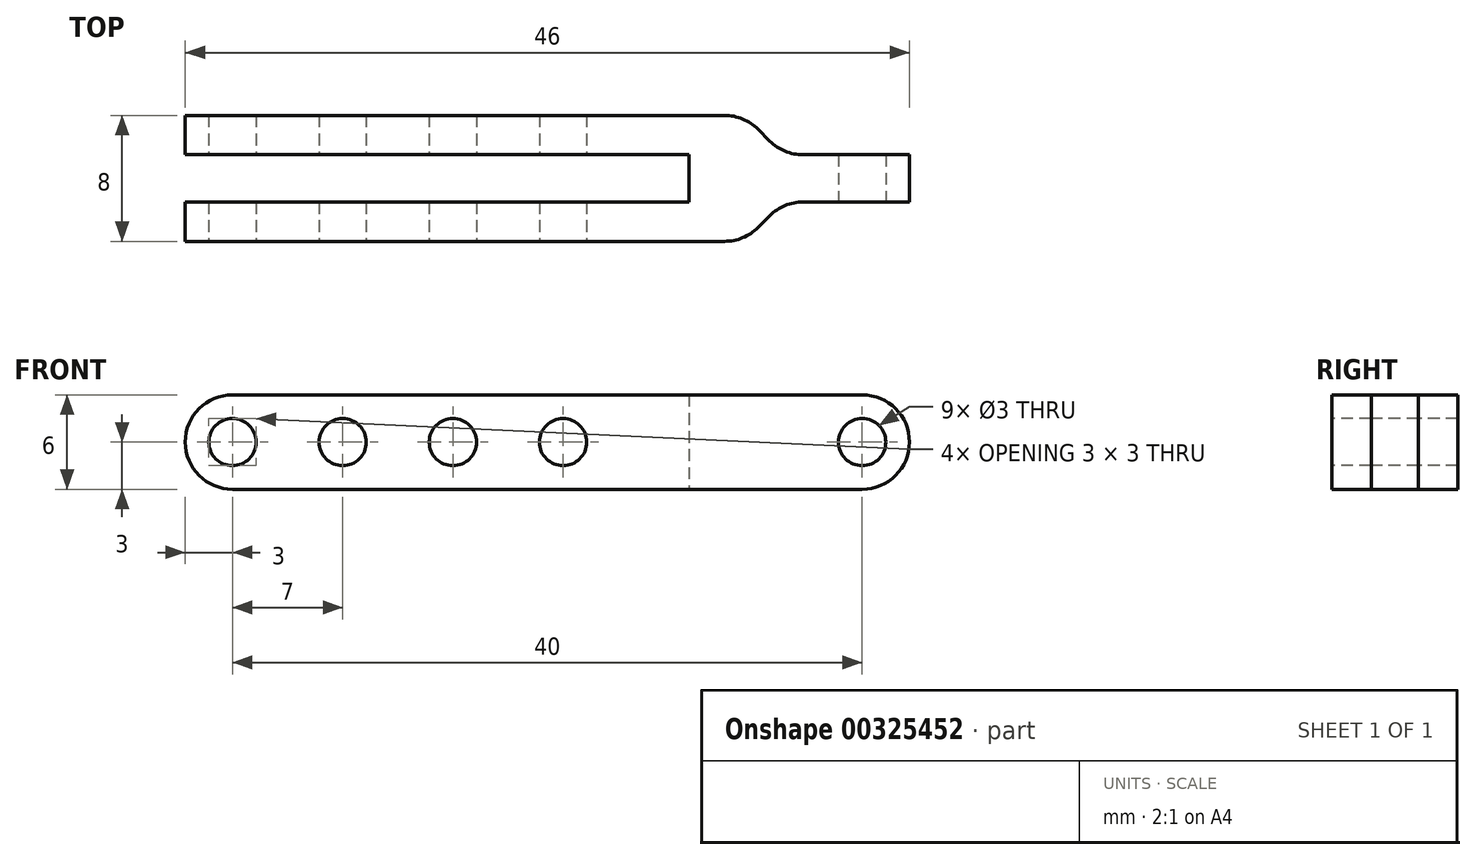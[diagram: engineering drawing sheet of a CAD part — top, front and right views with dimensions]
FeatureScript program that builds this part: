
annotation { "Feature Type Name" : "Feature", "Feature Type Description" : "" }
export const myFeature = defineFeature(function(context is Context, id is Id, definition is map)
    precondition{}
    {
        {
            var Q0;
            Q0=qCreatedBy(makeId("Top.planeOp"),FACE);
            var sketch = newSketch(context, id + "F0", { "sketchPlane" : qUnion([Q0])});
            skLineSegment(sketch, "E0.bottom", {"start": v(12.5, 4) * mm, "end": v(-23, 4) * mm});
            skLineSegment(sketch, "E0.top", {"start": v(12.5, -4) * mm, "end": v(-23, -4) * mm});
            skLineSegment(sketch, "E0.left", {"start": v(23, 1.5) * mm, "end": v(23, -1.5) * mm});
            skLineSegment(sketch, "E0.right", {"start": v(-23, 4) * mm, "end": v(-23, -4) * mm});
            skPoint(sketch, "E0.middle", {"position": v(0, 0) * mm});
            skLineSegment(sketch, "E1.bottom", {"start": v(-23, 1.5) * mm, "end": v(9, 1.5) * mm});
            skLineSegment(sketch, "E1.top", {"start": v(-23, -1.5) * mm, "end": v(9, -1.5) * mm});
            skLineSegment(sketch, "E1.right", {"start": v(9, 1.5) * mm, "end": v(9, -1.5) * mm});
            skLineSegment(sketch, "E2.bottom", {"start": v(23, 1.5) * mm, "end": v(15, 1.5) * mm});
            skLineSegment(sketch, "E2.top", {"start": v(23, -1.5) * mm, "end": v(15, -1.5) * mm});
            skLineSegment(sketch, "E3", {"start": v(15, 1.5) * mm, "end": v(12.5, 4) * mm});
            skLineSegment(sketch, "E4", {"start": v(15, -1.5) * mm, "end": v(12.5, -4) * mm});
            skPoint(sketch, "E5.orphan", {"position": v(23, 4) * mm});
            skPoint(sketch, "E6.orphan", {"position": v(23, -4) * mm});
            skSolve(sketch);
        }
        {
            var Q0;
            {var subQ2=sQuery(id+"F0.wireOp",EDGE,"E0.bottom");Q0=makeQuery(id+"F0.imprint","IMPRINT",FACE,{"disambiguationData":[TD([[makeQuery(id+"F0.imprint","IMPRINT",EDGE,{"derivedFrom":subQ2}),1.0]])]});}
            extrude(context, id + "F1", {"entities" : qUnion([Q0]), "depth" : 6 * mm});
        }
        {
            var Q0;
            {var subQ0=sQuery(id+"F0.wireOp",EDGE,"E0.right");Q0=makeQuery(id+"F1.opExtrude","CAP_EDGE",EDGE,{"disambiguationData":[OSD([subQ0]),TDD([makeQuery(id+"F0.imprint","IMPRINT",EDGE,{"disambiguationData":[TD([[makeQuery(id+"F0.imprint","INTERSECT",VERTEX,{"derivedFrom":[sQuery(id+"F0.wireOp",EDGE,"E0.top"),subQ0]}),1.0]])],"derivedFrom":subQ0})])],"isStart":false});}
            var Q1;
            {var subQ0=sQuery(id+"F0.wireOp",EDGE,"E0.right");Q1=makeQuery(id+"F1.opExtrude","CAP_EDGE",EDGE,{"disambiguationData":[OSD([subQ0]),TDD([makeQuery(id+"F0.imprint","IMPRINT",EDGE,{"disambiguationData":[TD([[makeQuery(id+"F0.imprint","INTERSECT",VERTEX,{"derivedFrom":[sQuery(id+"F0.wireOp",EDGE,"E0.bottom"),subQ0]}),-1.0]])],"derivedFrom":subQ0})])],"isStart":false});}
            var Q2;
            Q2=makeQuery(id+"F1.opExtrude","CAP_EDGE",EDGE,{"disambiguationData":[OSD([sQuery(id+"F0.wireOp",EDGE,"E0.left")])],"isStart":false});
            var Q3;
            Q3=makeQuery(id+"F1.opExtrude","CAP_EDGE",EDGE,{"disambiguationData":[OSD([sQuery(id+"F0.wireOp",EDGE,"E0.left")])],"isStart":true});
            var Q4;
            {var subQ0=sQuery(id+"F0.wireOp",EDGE,"E0.right");Q4=makeQuery(id+"F1.opExtrude","CAP_EDGE",EDGE,{"disambiguationData":[OSD([subQ0]),TDD([makeQuery(id+"F0.imprint","IMPRINT",EDGE,{"disambiguationData":[TD([[makeQuery(id+"F0.imprint","INTERSECT",VERTEX,{"derivedFrom":[sQuery(id+"F0.wireOp",EDGE,"E0.bottom"),subQ0]}),-1.0]])],"derivedFrom":subQ0})])],"isStart":true});}
            var Q5;
            {var subQ0=sQuery(id+"F0.wireOp",EDGE,"E0.right");Q5=makeQuery(id+"F1.opExtrude","CAP_EDGE",EDGE,{"disambiguationData":[OSD([subQ0]),TDD([makeQuery(id+"F0.imprint","IMPRINT",EDGE,{"disambiguationData":[TD([[makeQuery(id+"F0.imprint","INTERSECT",VERTEX,{"derivedFrom":[sQuery(id+"F0.wireOp",EDGE,"E0.top"),subQ0]}),1.0]])],"derivedFrom":subQ0})])],"isStart":true});}
            fillet(context, id + "F2", {"entities" : qUnion([Q0, Q1, Q2, Q3, Q4, Q5]), "radius" : 3 * mm, "tangentPropagation" : true, "allowEdgeOverflow" : false});
        }
        {
            var Q0;
            Q0=makeQuery(id+"F1.opExtrude","SWEPT_EDGE",EDGE,{"disambiguationData":[OSD([sQuery(id+"F0.wireOp",EDGE,"E0.bottom"),sQuery(id+"F0.wireOp",EDGE,"E3")])]});
            var Q1;
            Q1=makeQuery(id+"F1.opExtrude","SWEPT_EDGE",EDGE,{"disambiguationData":[OSD([sQuery(id+"F0.wireOp",EDGE,"E2.bottom"),sQuery(id+"F0.wireOp",EDGE,"E3")])]});
            var Q2;
            Q2=makeQuery(id+"F1.opExtrude","SWEPT_EDGE",EDGE,{"disambiguationData":[OSD([sQuery(id+"F0.wireOp",EDGE,"E2.top"),sQuery(id+"F0.wireOp",EDGE,"E4")])]});
            var Q3;
            Q3=makeQuery(id+"F1.opExtrude","SWEPT_EDGE",EDGE,{"disambiguationData":[OSD([sQuery(id+"F0.wireOp",EDGE,"E0.top"),sQuery(id+"F0.wireOp",EDGE,"E4")])]});
            fillet(context, id + "F3", {"entities" : qUnion([Q0, Q1, Q2, Q3]), "radius" : 3 * mm, "tangentPropagation" : true, "allowEdgeOverflow" : false});
        }
        {
            var Q0;
            Q0=makeQuery(id+"F1.opExtrude","SWEPT_FACE",FACE,{"disambiguationData":[OSD([sQuery(id+"F0.wireOp",EDGE,"E0.top")])]});
            var sketch = newSketch(context, id + "F4", { "sketchPlane" : qUnion([Q0])});
            skCircle(sketch, "E7", {"center": v(-20, 3) * mm, "radius": 1.5 * mm});
            skCircle(sketch, "E8", {"center": v(-13, 3) * mm, "radius": 1.5 * mm});
            skCircle(sketch, "E9", {"center": v(-6, 3) * mm, "radius": 1.5 * mm});
            skCircle(sketch, "E10", {"center": v(1, 3) * mm, "radius": 1.5 * mm});
            skSolve(sketch);
        }
        {
            var Q0;
            Q0=makeQuery(id+"F1.opExtrude","SWEPT_FACE",FACE,{"disambiguationData":[OSD([sQuery(id+"F0.wireOp",EDGE,"E2.top")])]});
            var sketch = newSketch(context, id + "F5", { "sketchPlane" : qUnion([Q0])});
            skCircle(sketch, "E11", {"center": v(20, 3) * mm, "radius": 1.5 * mm});
            skSolve(sketch);
        }
        {
            var Q0;
            Q0=makeQuery(id+"F4.imprint","IMPRINT",FACE,{"disambiguationData":[TD([[makeQuery(id+"F4.imprint","IMPRINT",EDGE,{"derivedFrom":sQuery(id+"F4.wireOp",EDGE,"E7")}),1.0]])]});
            var Q1;
            Q1=makeQuery(id+"F4.imprint","IMPRINT",FACE,{"disambiguationData":[TD([[makeQuery(id+"F4.imprint","IMPRINT",EDGE,{"derivedFrom":sQuery(id+"F4.wireOp",EDGE,"E8")}),1.0]])]});
            var Q2;
            Q2=makeQuery(id+"F4.imprint","IMPRINT",FACE,{"disambiguationData":[TD([[makeQuery(id+"F4.imprint","IMPRINT",EDGE,{"derivedFrom":sQuery(id+"F4.wireOp",EDGE,"E9")}),1.0]])]});
            var Q3;
            Q3=makeQuery(id+"F4.imprint","IMPRINT",FACE,{"disambiguationData":[TD([[makeQuery(id+"F4.imprint","IMPRINT",EDGE,{"derivedFrom":sQuery(id+"F4.wireOp",EDGE,"E10")}),1.0]])]});
            var Q4;
            Q4=makeQuery(id+"F5.imprint","IMPRINT",FACE,{"disambiguationData":[TD([[makeQuery(id+"F5.imprint","IMPRINT",EDGE,{"derivedFrom":sQuery(id+"F5.wireOp",EDGE,"E11")}),1.0]])]});
            extrude(context, id + "F6", {"entities" : qUnion([Q0, Q1, Q2, Q3, Q4]), "operationType" : NewBodyOperationType.REMOVE, "oppositeDirection" : true, "depth" : 25 * mm});
        }
    });
